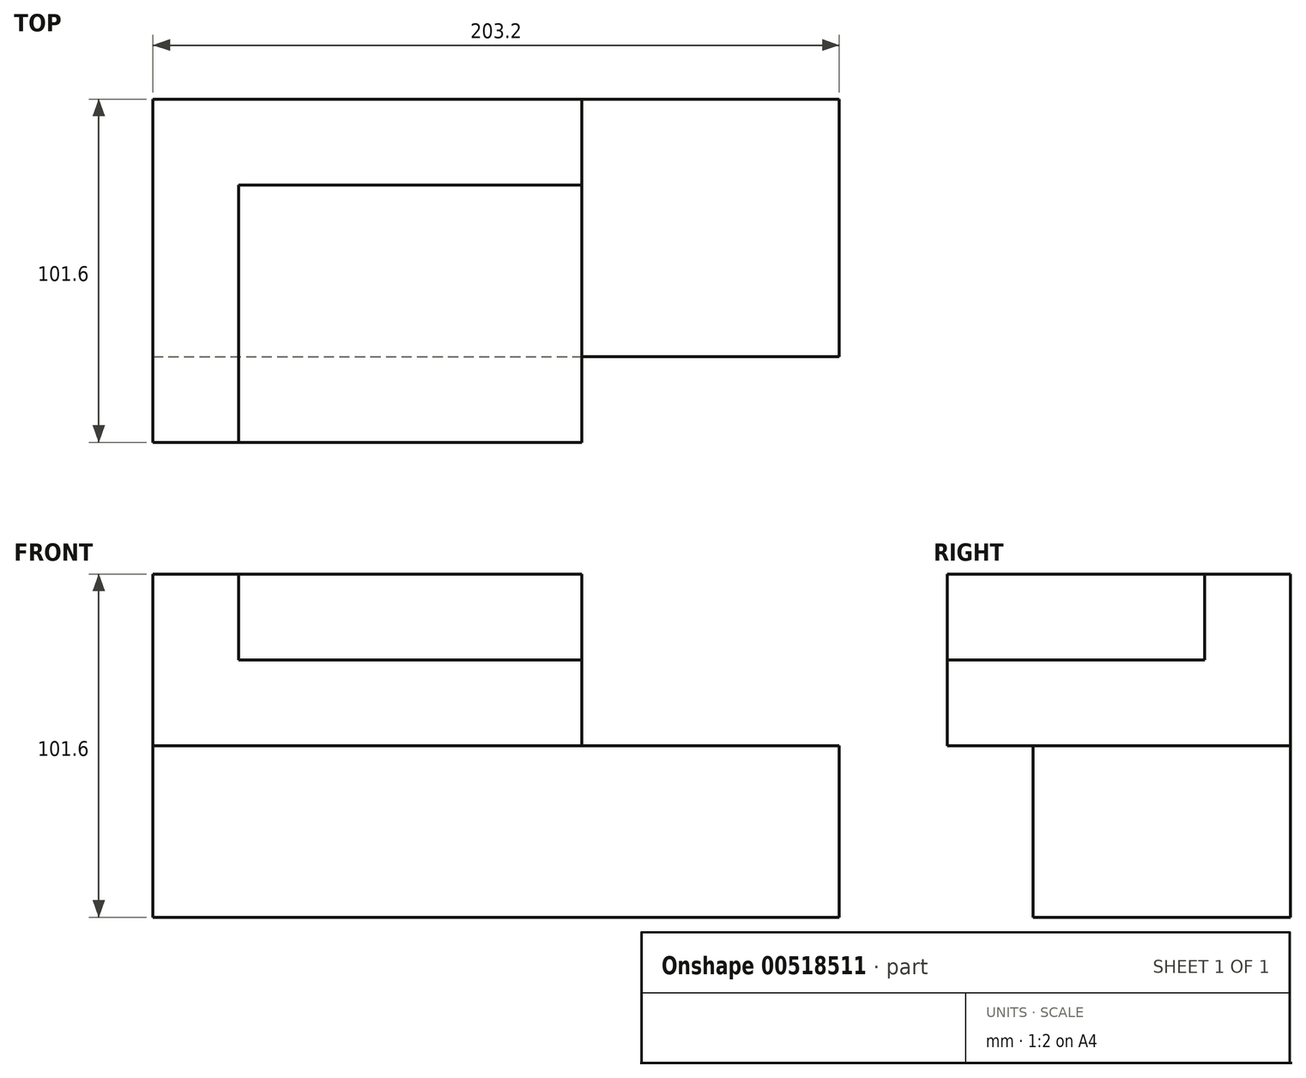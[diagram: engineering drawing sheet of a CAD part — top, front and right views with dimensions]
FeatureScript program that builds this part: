
annotation { "Feature Type Name" : "Feature", "Feature Type Description" : "" }
export const myFeature = defineFeature(function(context is Context, id is Id, definition is map)
    precondition{}
    {
        {
            var Q0;
            Q0=qCreatedBy(makeId("Front.planeOp"),FACE);
            var sketch = newSketch(context, id + "F0", { "sketchPlane" : qUnion([Q0])});
            skLineSegment(sketch, "E0.bottom", {"start": v(-142, -2.9) * mm, "end": v(61.2, -2.9) * mm});
            skLineSegment(sketch, "E0.top", {"start": v(-142, -53.7) * mm, "end": v(61.2, -53.7) * mm});
            skLineSegment(sketch, "E0.left", {"start": v(-142, -2.9) * mm, "end": v(-142, -53.7) * mm});
            skLineSegment(sketch, "E0.right", {"start": v(61.2, -2.9) * mm, "end": v(61.2, -53.7) * mm});
            skSolve(sketch);
        }
        {
            var Q0;
            Q0=qSketchRegion(id+"F0",true);
            extrude(context, id + "F1", {"entities" : qUnion([Q0]), "depth" : 76.2 * mm});
        }
        {
            var Q0;
            Q0=makeQuery(id+"F1.opExtrude","SWEPT_FACE",FACE,{"disambiguationData":[OSD([sQuery(id+"F0.wireOp",EDGE,"E0.bottom")])]});
            var sketch = newSketch(context, id + "F2", { "sketchPlane" : qUnion([Q0])});
            skLineSegment(sketch, "E1.bottom", {"start": v(-142, 0) * mm, "end": v(-15, 0) * mm});
            skLineSegment(sketch, "E1.top", {"start": v(-142, -101.6) * mm, "end": v(-15, -101.6) * mm});
            skLineSegment(sketch, "E1.left", {"start": v(-142, 0) * mm, "end": v(-142, -101.6) * mm});
            skLineSegment(sketch, "E1.right", {"start": v(-15, 0) * mm, "end": v(-15, -101.6) * mm});
            skSolve(sketch);
        }
        {
            var Q0;
            Q0=qSketchRegion(id+"F2",true);
            extrude(context, id + "F3", {"entities" : qUnion([Q0]), "operationType" : NewBodyOperationType.ADD, "depth" : 50.8 * mm});
        }
        {
            var Q0;
            Q0=makeQuery(id+"F3.opExtrude","CAP_FACE",FACE,{"disambiguationData":[OSD([sQuery(id+"F2.wireOp",EDGE,"E1.bottom"),sQuery(id+"F2.wireOp",EDGE,"E1.top"),sQuery(id+"F2.wireOp",EDGE,"E1.left"),sQuery(id+"F2.wireOp",EDGE,"E1.right")])],"isStart":false});
            var sketch = newSketch(context, id + "F4", { "sketchPlane" : qUnion([Q0])});
            skLineSegment(sketch, "E2.bottom", {"start": v(-15, -101.6) * mm, "end": v(-116.6, -101.6) * mm});
            skLineSegment(sketch, "E2.top", {"start": v(-15, -25.4) * mm, "end": v(-116.6, -25.4) * mm});
            skLineSegment(sketch, "E2.left", {"start": v(-15, -101.6) * mm, "end": v(-15, -25.4) * mm});
            skLineSegment(sketch, "E2.right", {"start": v(-116.6, -101.6) * mm, "end": v(-116.6, -25.4) * mm});
            skSolve(sketch);
        }
        {
            var Q0;
            Q0=qSketchRegion(id+"F4",true);
            extrude(context, id + "F5", {"entities" : qUnion([Q0]), "operationType" : NewBodyOperationType.REMOVE, "depth" : -25.4 * mm});
        }
    });
